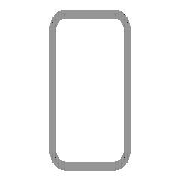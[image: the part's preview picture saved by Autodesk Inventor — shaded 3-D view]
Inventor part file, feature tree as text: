
AUTODESK INVENTOR PART (.ipt)
format: ipt  version: 2025 (Build 290162010, 162A)  size: 132,608 bytes
history: native  units: mm (DEFAULTED — no unit token found)
features: other x4, sketch x1, plane x1
ambient origin geometry x8: Origin, YZ Plane, XZ Plane, XY Plane, X Axis, Y Axis, Z Axis, Center Point
bodies: Solid1 (feature_tree), Body (feature_tree)
feature tree (6):
  parser-record x1  (decoder bookkeeping rows leaked as tree rows — omitted from the tree; the rows remain in map.json)
  other  "Driven Length"
  other  "Start Plane"
  other  "End Plane"
  sketch  "Sketch3"  dims[d3=1000.0mm d4=0.0mm d7=6.0mm d9=40.0mm d11=80.0mm d12=3.0mm d13=-0.0mm d14=1000.0mm d15=20.0mm d16=40.0mm d17=90.0deg d18=1000.0mm]
  plane  "Work Plane3"
